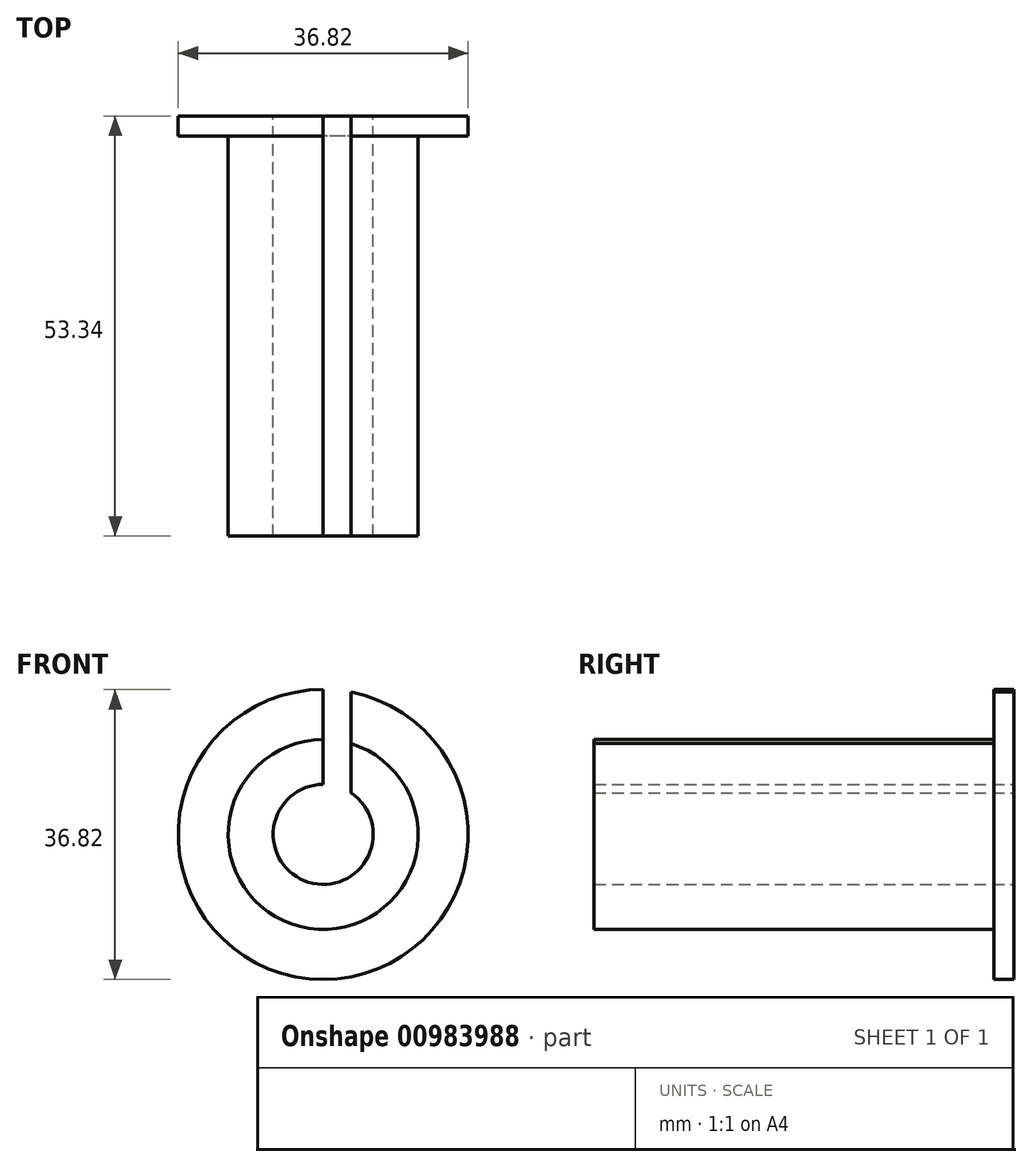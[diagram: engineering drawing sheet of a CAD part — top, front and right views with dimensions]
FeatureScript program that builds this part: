
annotation { "Feature Type Name" : "Feature", "Feature Type Description" : "" }
export const myFeature = defineFeature(function(context is Context, id is Id, definition is map)
    precondition{}
    {
        {
            var Q0;
            Q0=qCreatedBy(makeId("Top.planeOp"),FACE);
            var sketch = newSketch(context, id + "F0", { "sketchPlane" : qUnion([Q0])});
            skLineSegment(sketch, "E0", {"start": v(0, -15.61) * mm, "end": v(12.07, -15.61) * mm});
            skLineSegment(sketch, "E1", {"start": v(12.07, -15.61) * mm, "end": v(12.07, 35.19) * mm});
            skLineSegment(sketch, "E2", {"start": v(12.07, 35.19) * mm, "end": v(18.41, 35.19) * mm});
            skLineSegment(sketch, "E3", {"start": v(18.41, 35.19) * mm, "end": v(18.41, 37.73) * mm});
            skLineSegment(sketch, "E4", {"start": v(18.41, 37.73) * mm, "end": v(0, 37.73) * mm});
            skLineSegment(sketch, "E5", {"start": v(0, 37.73) * mm, "end": v(0, -15.61) * mm});
            skSolve(sketch);
        }
        {
            var Q0;
            Q0=makeQuery(id+"F0.imprint","IMPRINT",FACE,{"disambiguationData":[TD([[makeQuery(id+"F0.imprint","IMPRINT",EDGE,{"derivedFrom":sQuery(id+"F0.wireOp",EDGE,"E0")}),1.0]])]});
            var Q1;
            Q1=sQuery(id+"F0.wireOp",EDGE,"E5");
            revolve(context, id + "F1", {"surfaceOperationType" : NewSurfaceOperationType.NEW, "entities" : qUnion([Q0]), "axis" : qUnion([Q1]), "revolveType" : RevolveType.FULL});
        }
        {
            var Q0;
            Q0=makeQuery(id+"F1.opRevolve","SWEPT_FACE",FACE,{"disambiguationData":[OSD([sQuery(id+"F0.wireOp",EDGE,"E4")])]});
            var sketch = newSketch(context, id + "F2", { "sketchPlane" : qUnion([Q0])});
            skCircle(sketch, "E6", {"center": v(0, 0) * mm, "radius": 6.35 * mm});
            skSolve(sketch);
        }
        {
            var Q0;
            Q0=qSketchRegion(id+"F2",true);
            extrude(context, id + "F3", {"entities" : qUnion([Q0]), "operationType" : NewBodyOperationType.REMOVE, "oppositeDirection" : true, "depth" : 101.6 * mm, "offsetDistance" : 25.4 * mm});
        }
        {
            var Q0;
            Q0=makeQuery(id+"F1.opRevolve","SWEPT_FACE",FACE,{"disambiguationData":[OSD([sQuery(id+"F0.wireOp",EDGE,"E4")])]});
            var sketch = newSketch(context, id + "F4", { "sketchPlane" : qUnion([Q0])});
            skLineSegment(sketch, "E7", {"start": v(0, 18.41) * mm, "end": v(0, 6.35) * mm});
            skLineSegment(sketch, "E8", {"start": v(0, 6.35) * mm, "end": v(-3.53, 4.9) * mm});
            skLineSegment(sketch, "E9", {"start": v(-3.53, 4.9) * mm, "end": v(-3.53, 18.86) * mm});
            skLineSegment(sketch, "E10", {"start": v(-3.53, 18.86) * mm, "end": v(0, 18.86) * mm});
            skLineSegment(sketch, "E11", {"start": v(0, 18.86) * mm, "end": v(0, 18.41) * mm});
            skSolve(sketch);
        }
        {
            var Q0;
            {var subQ0=sQuery(id+"F4.wireOp",EDGE,"E7");Q0=makeQuery(id+"F4.imprint","IMPRINT",FACE,{"disambiguationData":[TD([[makeQuery(id+"F4.imprint","IMPRINT",EDGE,{"derivedFrom":subQ0}),-1.0]])]});}
            extrude(context, id + "F5", {"entities" : qUnion([Q0]), "operationType" : NewBodyOperationType.REMOVE, "oppositeDirection" : true, "depth" : 127 * mm, "offsetDistance" : 25.4 * mm});
        }
    });
